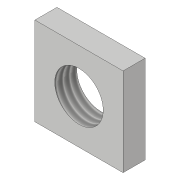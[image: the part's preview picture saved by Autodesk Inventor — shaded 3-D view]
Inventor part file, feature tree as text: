
AUTODESK INVENTOR PART (.ipt)
format: ipt  version: 2019 (Build 230136000, 136)  size: 89,088 bytes
history: native  units: mm
features: extrude x2, sketch x2, thread x1
ambient origin geometry x8: Origin, YZ Plane, XZ Plane, XY Plane, X Axis, Y Axis, Z Axis, Center Point
bodies: Solid1 (feature_tree)
feature tree (5):
  extrude  "Extrusion1"  Depth=20.0mm
  extrude  "Extrusion2"  Depth=10.0mm
  thread  "Thread1"  [1 undecoded]
  sketch  "Sketch1"  dims[d0=20.0mm d1=20.0mm]
  sketch  "Sketch2"  dims[d2=5.0mm d3=0.0mm d4=10.0mm d5=10.0mm d6=11.0mm d7=0.0mm d8=0.0mm d9=10.0mm d10=0.0mm]
note: 1 required parameter value undecoded (feature->parameter linkage not recoverable at this tier; creation-order binding heuristic only, values carry confidence <= 0.55)
